# Revit family: Medical_All_Hill-Rom_Centrella™-Smart+Bed
name_source: partatom
category: Specialty Equipment
revit_build: Autodesk Revit Architecture 2015 (Build: 20140606_1530(x64)
units: mm (PartAtom-declared; Revit-internal decimal feet)

## types (1)
- Centrella™ Smart+ Bed
    "Comfort Edition 40"" Width" = Yes
    5th Wheel Steering = Yes
    Accessory Outlet = Yes
    Actual Foot Angle = 0.25°
    Actual Head Angle = 0.25°
    Advanced SlideGuard® technology = Yes
    Apparent Load = 0 VA
    BIMobject category = All
    BIMobject category code = medical-all
    BIMobject main category = Medical
    BIMobject main category code = medical
    Battery Backup = Yes
    Bed Exit Silence = Yes
    Bed Height maximum = 2' - 8 1/2"
    Bed Height minimum = 1' - 2 1/2"
    Brake-Not-Set Alert = Yes
    Brand url = https://construction.hill-rom.com
    Bumpers = Plastic-Hill-Rom-Light Blue
    CNT155 CORE Surface = 35.5"W x 76"-88"L x 6"H
    CNT255 PRO Surface = 35.5" or 38.5"W x 76"-88"L x 7"H
    CNT355 MAX Surface = 35.5" or 38.5"W x 76"-88"L x 8"H
    Caster size = 0' - 5"
    Caster type = Central Locking System
    Centrella™ MAX Powered Air Surface = Yes
    Dampen Emergency CPR = Yes
    Date of publishing = 8/10/2018
    Description = Electric Med-Surg Patient Bed
    Design country = United States
    Device Storage Area = Yes
    Digital Angle Indicator = Yes
    Drainage Bag Holder = Yes
    Edition number = 1
    Enhanced 3-Mode Bed Exit = Yes
    Finish = Plastic-Hill-Rom-Light Beige
    FlexAfoot™ Powered Bed Extension = Yes
    Foley Position Limit = Yes
    Foot Angle = 0.00°
    Foot section inclination = 50.00°
    Four Corner Brake and Steer = Yes
    Four IV Pole Sockets (located at each corner) = Yes
    Frequency = 0 Hz
    Frequency Range = 50-60 Hz
    Full Load Current = 0 A
    Graphical Caregiver Interface (GCI)® touchscreen (right side) = Yes
    Handles_Material = Plastic-Hill-Rom-Blue
    Head Angle = 0.00°
    Head section inclination = 65.00°
    Head-End Traction = Yes
    IFC Classification = Furniture
    IllumiGuide™ Siderail Handgrip = Yes
    Installation instructions = https://construction.hill-rom.com
    Integrated Restraint Holders = Yes
    Integrated Urinal Holders = Yes
    IntelliDrive® Powered Transport = Yes
    Line and Cord Management = Yes
    Lockout Controls = Yes
    Manufacturer = Hill-Rom Co.
    Manufacturer country = United States
    Manufacturer name = Hill-Rom
    Masterformat 2014 Code = 12 54 00
    Masterformat 2014 Description = Hospitality Furniture
    Mattress = Textile-Hill-Rom-Matress
    Mattress Height = 0' - 6"
    Max Amperage = 10 A
    Model = CNT155 / CNT255 / CNT355
    Motion-Activated Nightlight = Yes
    Nominal height = 0' - 0"
    Nominal width = 0' - 0"
    Nurse Call = Yes
    OmniClass Code = 23-25 45 11 11
    OmniClass Description = Patient Beds
    One Button Chair = Yes
    One-button Patient Stand Assist = Yes
    Overall Width = 3' - 4"
    Overall Width (Comfort Edition) = 3' - 7"
    Overall length(foot section extended) = 8' - 2 11/16"
    Overall length(foot section retracted) = 7' - 2 11/16"
    Patient HOB Angle Display = Yes
    Patient Pendant = Yes
    Patient weight range = 70 – 500 lbs (32 – 227 kg)
    Power Factor = 1
    Product Guid = c47ba607-46e1-44b6-91f1-ed641e753be3
    Product SKU = Centrella-med-surg-bed
    Product certification = https://centrellabed.com
    Product data url = https://bimobject.com
    Product family = Patient Beds
    Product group = Centrella™ Smart+ Bed
    Product url = https://www.hill-rom.ca
    QR code = http://bimobject.com
    Reverse Trend position (max) = 15.00°
    Safe Working Load = 650 lbs (295 kg)
    SafeView®+ System = Yes
    Scale (kg/lbs) = Yes
    Second Graphical Caregiver Interface(GCI)® touchscreen = Yes
    Second Patient Pendant = Yes
    Smart Bed Ready (SideCom® Required) = Yes
    Technical description = https://construction.hill-rom.com
    Thigh section inclination = 25.00°
    Trendelenburg position (max) = 15.00°
    Trendelenburg/Reverse Trendelenburg = Yes
    Type Comments = Electric Med-Surg Patient Bed
    UNSPSC Code = 56
    URL = www.hill-rom.com
    USB Charging = Yes
    Uniclass 1.4 Code = L8522
    Uniclass 1.4 Description = Hospital beds
    Uniclass 2015 Code = Pr_40_50_06_39
    Uniclass 2015 Name = Hospital beds
    Universal TV and Lighting Controls = Yes
    Verbal Safety Prompts = Yes
    Voltage = 0 V
    Voltage Range = 100-240 V
    Wheels = Plastic-Hill-Rom-Light Blue
    WiFi = Yes
    Youtube clip = https://www.hill-rom.ca

## geometry (parser evidence)
native form markers: Blend x6, Sweep x3
no freeform markers — native parametric forms only
